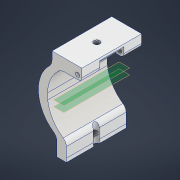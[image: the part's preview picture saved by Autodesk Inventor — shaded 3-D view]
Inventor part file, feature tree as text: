
AUTODESK INVENTOR PART (.ipt)
format: ipt  version: 2021 (Build 250183000, 183)  size: 216,064 bytes
history: native  units: in
note: dims shown in document units (in); Inventor stores cm internally (conversion verified against a paired STEP export)
features: fillet x5, sketch x5, extrude x4, hole x2, plane x2, split x2
ambient origin geometry x8: Origin, YZ Plane, XZ Plane, XY Plane, X Axis, Y Axis, Z Axis, Center Point
bodies: Solid1 (feature_tree)
feature tree (20):
  extrude  "Extrusion1"  Depth=3.937in TaperAngle=0.0deg
  extrude  "Extrusion6"  Depth=1.9685in
  extrude  "Extrusion8"  Depth=1.1811in
  extrude  "Extrusion9"  Depth=0.2756in
  hole  "Hole4"  [1 undecoded]
  fillet  "Fillet1"  Radius=3.937in
  fillet  "Fillet2"  Radius=0.5118in
  fillet  "Fillet3"  Radius=0.5906in
  fillet  "Fillet4"  Radius=0.3937in
  fillet  "Fillet5"  Radius=0.2362in
  plane  "Work Plane2"
  plane  "Work Plane3"
  split  "Split3"
  split  "Split4"
  hole  "Hole5"  [1 undecoded]
  sketch  "Sketch2"  dims[d1=1.9685in d2=3.937in d3=0.0in]
  sketch  "Sketch12"  dims[d56=3.937in d57=1.9685in]
  sketch  "Sketch18"  dims[d58=2.3622in d59=1.1811in]
  sketch  "Sketch19"  dims[d62=3.937in d63=0.0in d82=0.2756in]
  sketch  "Sketch20"  dims[d83=0.2756in d84=0.2756in d85=3.937in d86=0.0in d89=0.5118in d90=0.0in d91=0.5906in d92=0.3937in d93=0.3937in d94=0.2362in d95=0.3937in d96=0.1181in d97=90.0deg d98=0.315in d99=0.8108in d102=0.2362in d103=2.3622in d104=0.5512in d105=0.7874in d106=0.7874in d108=0.6299in d109=0.6299in d110=0.6299in d111=0.4724in d112=0.5906in d113=0.0787in d114=-3.3465in d115=-2.9528in d116=1.9685in d117=3.937in d118=1.9685in d119=0.9843in d120=0.3937in d121=0.2362in d122=0.1575in d123=0.0787in d124=90.0deg d125=0.315in d126=0.8108in d64=0.0197in d65=0.0344in d66=0.0197in d67=0.0344in d75=0.0394in d76=0.0394in d77=0.0394in d78=0.0059in d79=0.0098in d80=0.0148in d81=0.5635in]
note: 2 required parameter values undecoded (feature->parameter linkage not recoverable at this tier; creation-order binding heuristic only, values carry confidence <= 0.55)
